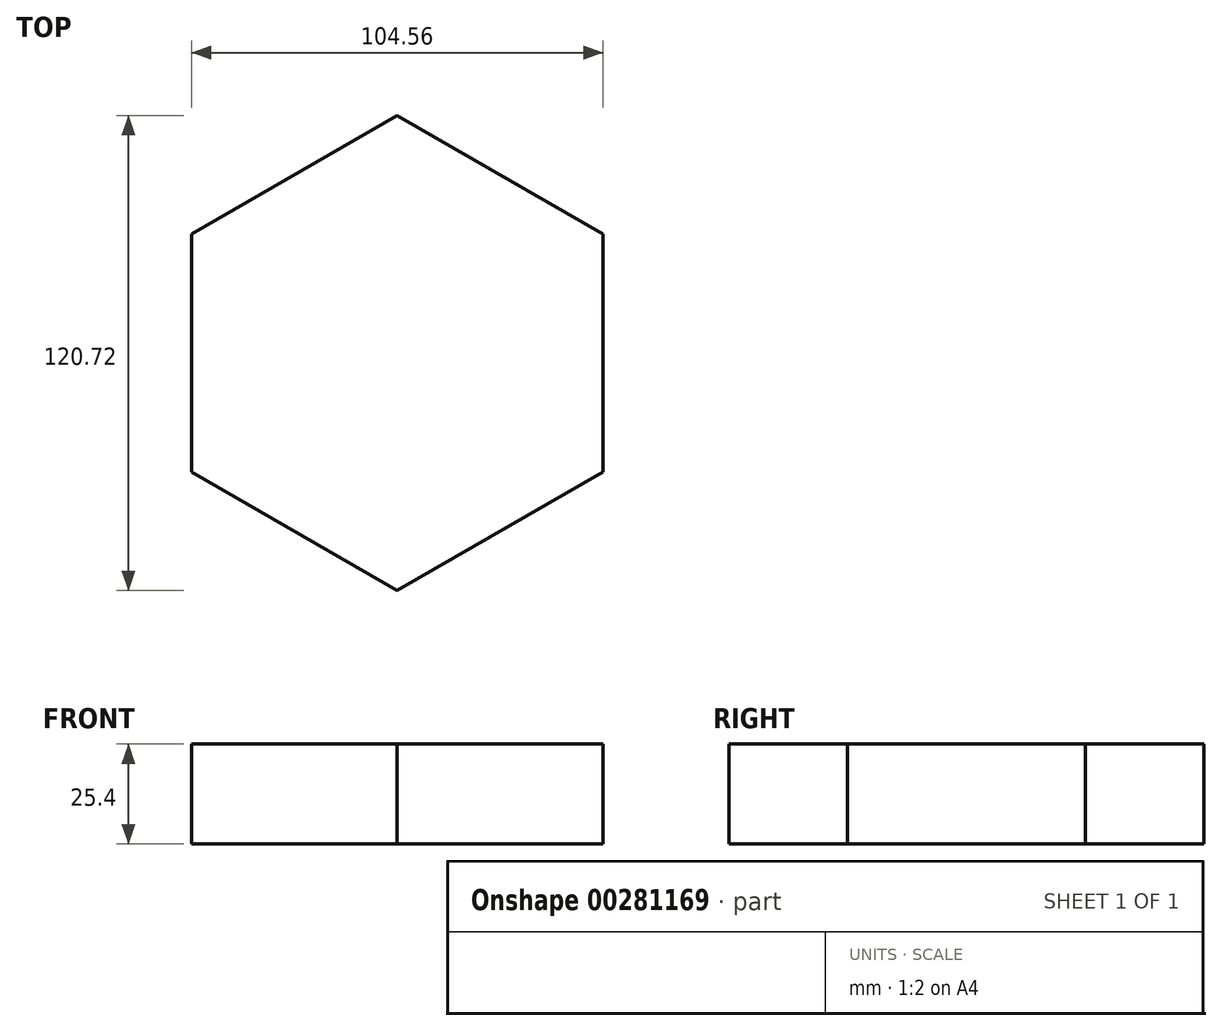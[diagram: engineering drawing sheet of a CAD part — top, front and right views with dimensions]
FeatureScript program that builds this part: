
annotation { "Feature Type Name" : "Feature", "Feature Type Description" : "" }
export const myFeature = defineFeature(function(context is Context, id is Id, definition is map)
    precondition{}
    {
        {
            var Q0;
            Q0=qCreatedBy(makeId("Top.planeOp"),FACE);
            var sketch = newSketch(context, id + "F0", { "sketchPlane" : qUnion([Q0])});
            skCircle(sketch, "E0.cCircle", {"center": v(0, 0) * mm, "radius": 52.28 * mm, "construction": true});
            skLineSegment(sketch, "E0.0", {"start": v(52.28, 30.18) * mm, "end": v(52.28, -30.18) * mm});
            skLineSegment(sketch, "E0.1", {"start": v(52.28, -30.18) * mm, "end": v(0, -60.36) * mm});
            skLineSegment(sketch, "E0.2", {"start": v(0, -60.36) * mm, "end": v(-52.28, -30.18) * mm});
            skLineSegment(sketch, "E0.3", {"start": v(-52.28, -30.18) * mm, "end": v(-52.28, 30.18) * mm});
            skLineSegment(sketch, "E0.4", {"start": v(-52.28, 30.18) * mm, "end": v(0, 60.36) * mm});
            skLineSegment(sketch, "E0.5", {"start": v(0, 60.36) * mm, "end": v(52.28, 30.18) * mm});
            skPoint(sketch, "E0.0.midPoint", {"position": v(52.28, 0) * mm});
            skSolve(sketch);
        }
        {
            var Q0;
            Q0 = qSketchRegion(id + "F0", true);
            extrude(context, id + "F1", {"entities" : qUnion([Q0]), "depth" : 25.4 * mm});
        }
    });
